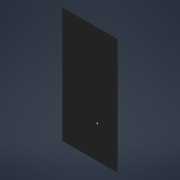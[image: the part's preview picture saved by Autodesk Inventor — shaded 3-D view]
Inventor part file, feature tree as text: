
AUTODESK INVENTOR PART (.ipt)
format: ipt  version: 2022 (Build 260153000, 153)  size: 87,552 bytes
history: imported  units: in
note: dims shown in document units (in); Inventor stores cm internally (conversion verified against a paired STEP export)
features: sketch x1, imported_body x1
ambient origin geometry x8: Origin, YZ Plane, XZ Plane, XY Plane, X Axis, Y Axis, Z Axis, Center Point
bodies: Solid1 (imported_parasolid), Body1 (imported_parasolid)
feature tree (2):
  sketch  "Sketch1"
  imported_body  NMx_Import_Brep_tag  [imported B-rep: ~6 faces, bbox_mm=[18.2624, 38.3412, 0.1]]
